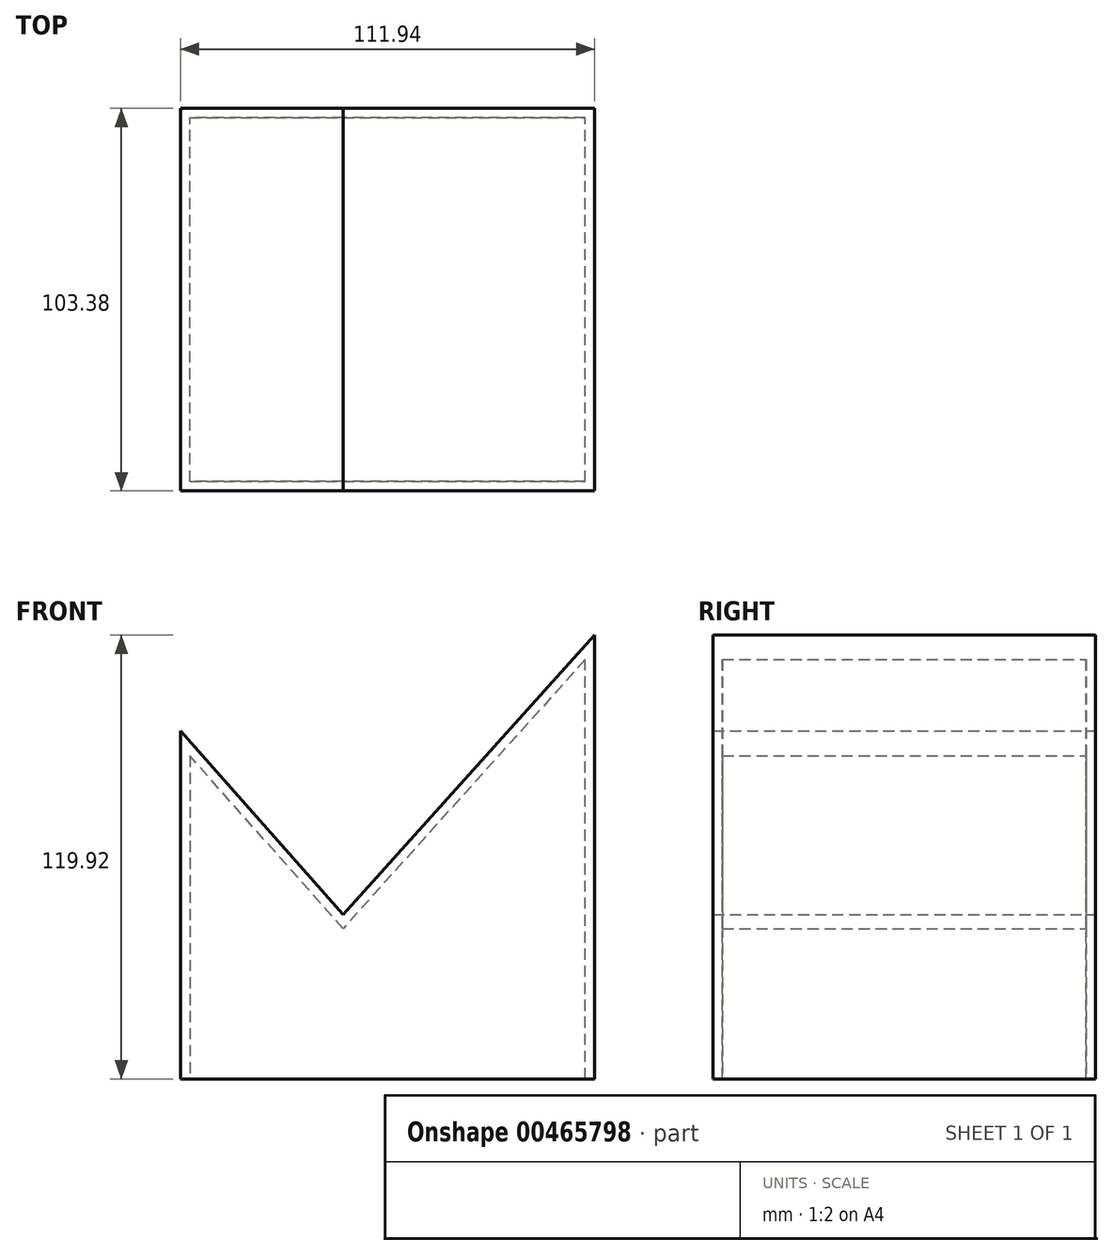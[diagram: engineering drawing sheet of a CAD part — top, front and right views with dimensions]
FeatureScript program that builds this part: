
annotation { "Feature Type Name" : "Feature", "Feature Type Description" : "" }
export const myFeature = defineFeature(function(context is Context, id is Id, definition is map)
    precondition{}
    {
        {
            var Q0;
            Q0=qCreatedBy(makeId("Front.planeOp"),FACE);
            var sketch = newSketch(context, id + "F0", { "sketchPlane" : qUnion([Q0])});
            skLineSegment(sketch, "E0", {"start": v(0, 0) * mm, "end": v(40.18, 0) * mm});
            skLineSegment(sketch, "E1", {"start": v(40.18, 0) * mm, "end": v(40.18, 119.92) * mm});
            skLineSegment(sketch, "E2", {"start": v(40.18, 119.92) * mm, "end": v(-27.82, 44.43) * mm});
            skLineSegment(sketch, "E3", {"start": v(-27.82, 44.43) * mm, "end": v(-71.76, 94) * mm});
            skLineSegment(sketch, "E4", {"start": v(-71.76, 94) * mm, "end": v(-71.76, 0) * mm});
            skLineSegment(sketch, "E5", {"start": v(-71.76, 0) * mm, "end": v(0, 0) * mm});
            skSolve(sketch);
        }
        {
            var Q0;
            Q0=makeQuery(id+"F0.imprint","IMPRINT",FACE,{"disambiguationData":[TD([[makeQuery(id+"F0.imprint","IMPRINT",EDGE,{"derivedFrom":sQuery(id+"F0.wireOp",EDGE,"E0")}),1.0]])]});
            extrude(context, id + "F1", {"entities" : qUnion([Q0]), "depth" : 103.38 * mm});
        }
        {
            var Q0;
            Q0=makeQuery(id+"F1.opExtrude","SWEPT_FACE",FACE,{"disambiguationData":[OSD([sQuery(id+"F0.wireOp",EDGE,"E0"),sQuery(id+"F0.wireOp",EDGE,"E5")])]});
            shell(context, id + "F2", {"entities" : qUnion([Q0]), "thickness" : 2.54 * mm});
        }
    });
